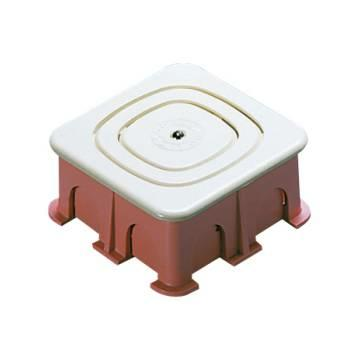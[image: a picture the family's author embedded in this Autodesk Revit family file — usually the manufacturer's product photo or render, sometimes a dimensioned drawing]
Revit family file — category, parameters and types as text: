
# Revit family: Building-ContenitoriIncasso-GEWISS-24SC-SCATOLE-INCASSO_TELEFONICA
name_source: partatom
category: Apparecchi elettrici
revit_build: Autodesk Revit 2016 (Build: 20161004_0715(x64)
units: mm (PartAtom-declared; Revit-internal decimal feet)

## family parameters
Condiviso = Sì
Host = Muro
Mantenere orientamento annotazione = Sì
Numero OmniClass = 23.80.30.14.24
Punto di calcolo locali = Sì
Quota connettore circolare = Usa diametro
Sempre verticale = Sì
Taglio con vuoti quando caricato = Sì
Tipo di parte = Normale
Titolo OmniClass = Junction Boxes

## types (1)
- GW24221 - Scatola impianti telefonici tradizionale
    Catalogo = BUILDING
    Catalogo Serie = 24SC
    Codice EAN = 8011564016644
    Codice Electrocod = 0210
    Colore coperchio = Avorio
    Descrizione = SCATOLA IMPIANTI TELEFONICI TRADIZIONALE
    Dim. esterne BxHxP (mm) = 68x68x30
    IDF = efa84f44-4c30-41bc-a0fa-5ad230894c88
    IDT = 72fbfc7d-f9ad-4603-970f-2f3f2820655a
    Immagine tipo = GW24221.jpg
    Installazione = Incasso
    Modello = GW24221
    Per Pareti = Muratura
    Per installazioni di tipo = Tradizionale
    Produttore = GEWISS S.p.A.
    SEO = Scatola
    Scheda Tecnica = https://www.gewiss.com
    URL = https://www.gewiss.com
    Versione file RFA = 19.0
